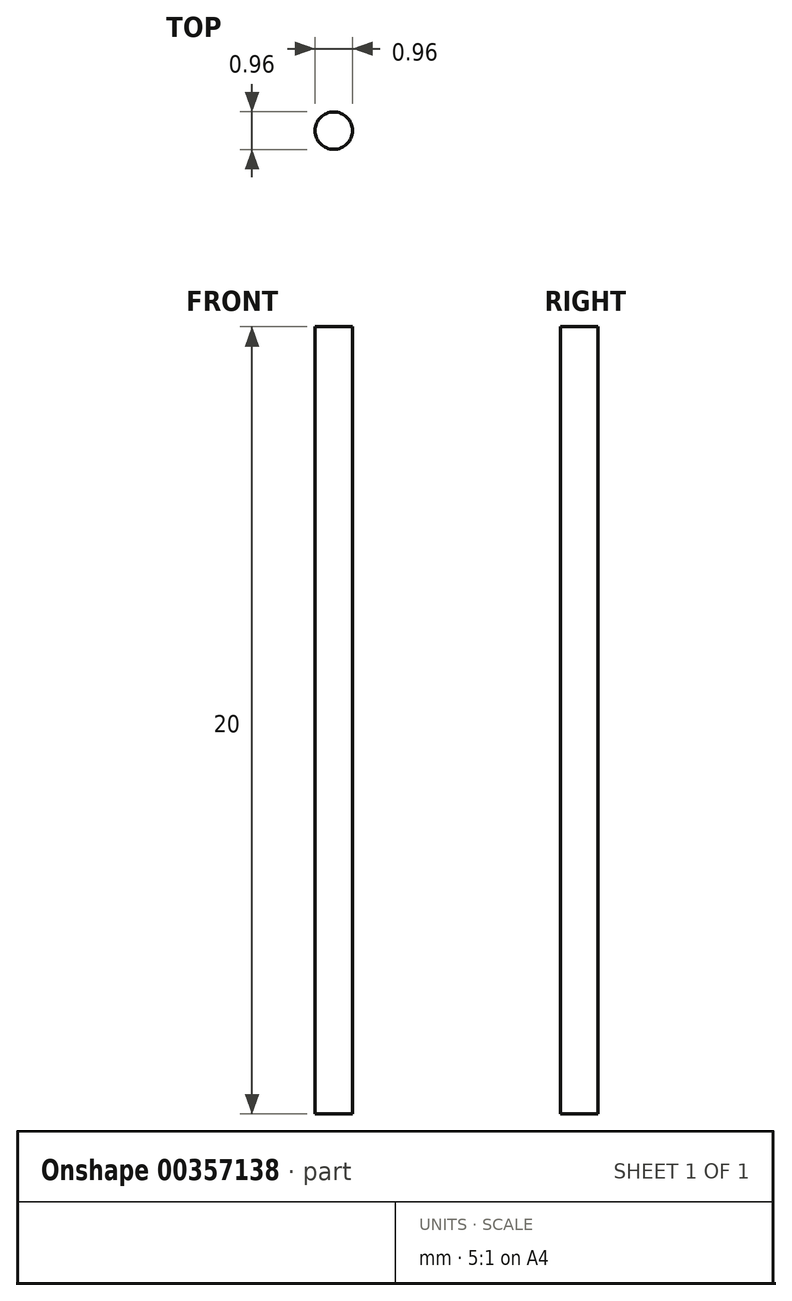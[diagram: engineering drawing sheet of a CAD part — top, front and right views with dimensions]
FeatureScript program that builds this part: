
annotation { "Feature Type Name" : "Feature", "Feature Type Description" : "" }
export const myFeature = defineFeature(function(context is Context, id is Id, definition is map)
    precondition{}
    {
        {
            var Q0;
            Q0=qCreatedBy(makeId("Top.planeOp"),FACE);
            var sketch = newSketch(context, id + "F0", { "sketchPlane" : qUnion([Q0])});
            skCircle(sketch, "E0", {"center": v(0, 0) * mm, "radius": 0.47 * mm});
            skSolve(sketch);
        }
        {
            var Q0;
            Q0 = qSketchRegion(id + "F0", true);
            extrude(context, id + "F1", {"entities" : qUnion([Q0]), "endBound" : BoundingType.SYMMETRIC, "depth" : 20 * mm});
        }
    });
